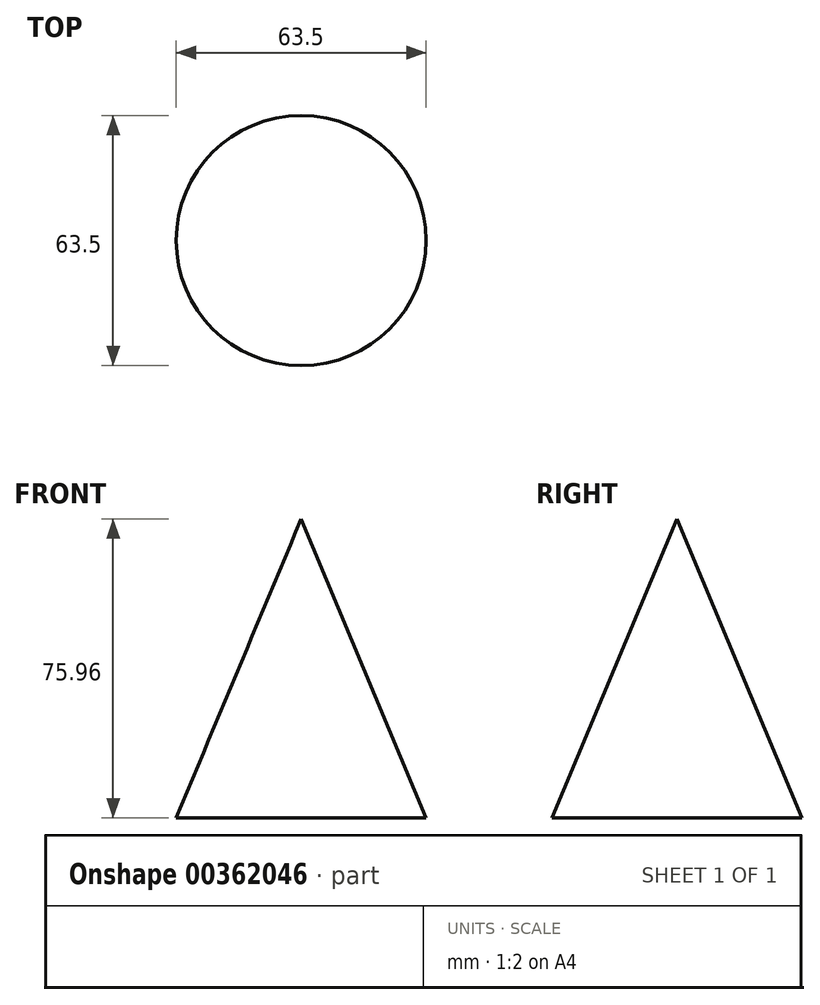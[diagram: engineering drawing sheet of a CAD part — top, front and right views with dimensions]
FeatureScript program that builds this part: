
annotation { "Feature Type Name" : "Feature", "Feature Type Description" : "" }
export const myFeature = defineFeature(function(context is Context, id is Id, definition is map)
    precondition{}
    {
        {
            var Q0;
            Q0=qCreatedBy(makeId("Front.planeOp"),FACE);
            var sketch = newSketch(context, id + "F0", { "sketchPlane" : qUnion([Q0])});
            skLineSegment(sketch, "E0", {"start": v(0, 0) * mm, "end": v(0, 75.96) * mm});
            skLineSegment(sketch, "E1", {"start": v(0, 75.96) * mm, "end": v(-31.75, 0) * mm});
            skLineSegment(sketch, "E2", {"start": v(-31.75, 0) * mm, "end": v(0, 0) * mm});
            skLineSegment(sketch, "E3", {"start": v(0, 0) * mm, "end": v(31.75, 0) * mm});
            skLineSegment(sketch, "E4", {"start": v(31.75, 0) * mm, "end": v(0, 75.96) * mm});
            skSolve(sketch);
        }
        {
            var Q0;
            Q0=makeQuery(id+"F0.imprint","IMPRINT",FACE,{"disambiguationData":[TD([[makeQuery(id+"F0.imprint","IMPRINT",EDGE,{"derivedFrom":sQuery(id+"F0.wireOp",EDGE,"E0")}),-1.0]])]});
            var Q1;
            Q1=sQuery(id+"F0.wireOp",EDGE,"E0");
            revolve(context, id + "F1", {"entities" : qUnion([Q0]), "axis" : qUnion([Q1]), "revolveType" : RevolveType.FULL});
        }
    });
